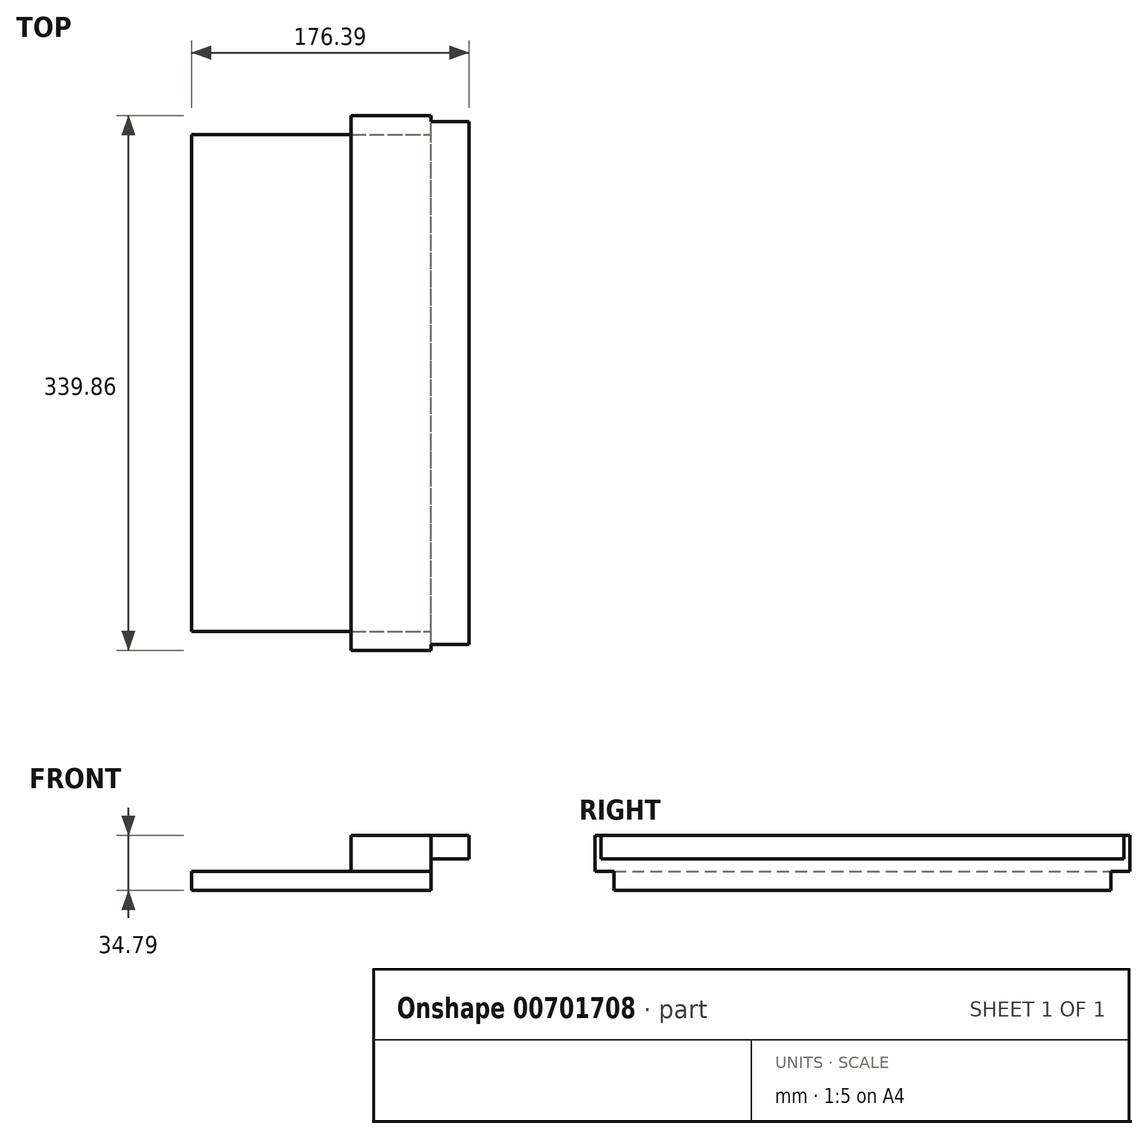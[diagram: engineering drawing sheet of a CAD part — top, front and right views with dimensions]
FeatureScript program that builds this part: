
annotation { "Feature Type Name" : "Feature", "Feature Type Description" : "" }
export const myFeature = defineFeature(function(context is Context, id is Id, definition is map)
    precondition{}
    {
        {
            var Q0;
            Q0=qCreatedBy(makeId("Front.planeOp"),FACE);
            var sketch = newSketch(context, id + "F0", { "sketchPlane" : qUnion([Q0])});
            skLineSegment(sketch, "E0", {"start": v(-72.73, 57.8) * mm, "end": v(-3.41, 57.8) * mm});
            skLineSegment(sketch, "E1", {"start": v(-3.41, 57.8) * mm, "end": v(-3.41, 3.04) * mm});
            skLineSegment(sketch, "E2", {"start": v(-3.41, 3.04) * mm, "end": v(-73.1, 3.04) * mm});
            skLineSegment(sketch, "E3", {"start": v(-73.1, 3.04) * mm, "end": v(-72.73, 57.8) * mm});
            skSolve(sketch);
        }
        {
            var Q0;
            Q0=makeQuery(id+"F0.imprint","IMPRINT",FACE,{"disambiguationData":[TD([[makeQuery(id+"F0.imprint","IMPRINT",EDGE,{"derivedFrom":sQuery(id+"F0.wireOp",EDGE,"E0")}),-1.0]])]});
            extrude(context, id + "F1", {"entities" : qUnion([Q0]), "depth" : 42.93 * mm, "offsetDistance" : 25.4 * mm});
        }
        {
            var Q0;
            Q0=qCreatedBy(makeId("Front.planeOp"),FACE);
            var sketch = newSketch(context, id + "F2", { "sketchPlane" : qUnion([Q0])});
            skCircle(sketch, "E4", {"center": v(-37.15, -45.63) * mm, "radius": 15.91 * mm});
            skSolve(sketch);
        }
        {
            var Q0;
            Q0=makeQuery(id+"F2.imprint","IMPRINT",FACE,{"disambiguationData":[TD([[makeQuery(id+"F2.imprint","IMPRINT",EDGE,{"derivedFrom":sQuery(id+"F2.wireOp",EDGE,"E4")}),1.0]])]});
            extrude(context, id + "F3", {"entities" : qUnion([Q0]), "depth" : 217.93 * mm, "offsetDistance" : 25.4 * mm});
        }
        {
            var Q0;
            Q0=makeQuery(id+"F3.opExtrude","SWEPT_BODY",BODY,{"disambiguationData":[OSD([sQuery(id+"F2.wireOp",EDGE,"E4")])]});
            var Q1;
            Q1=makeQuery(id+"F1.opExtrude","SWEPT_BODY",BODY,{"disambiguationData":[OSD([sQuery(id+"F0.wireOp",EDGE,"E0"),sQuery(id+"F0.wireOp",EDGE,"E1"),sQuery(id+"F0.wireOp",EDGE,"E2"),sQuery(id+"F0.wireOp",EDGE,"E3")])]});
            deleteBodies(context, id + "F4", {"entities" : qUnion([Q0, Q1])});
        }
        {
            var Q0;
            Q0=qCreatedBy(makeId("Front.planeOp"),FACE);
            var sketch = newSketch(context, id + "F5", { "sketchPlane" : qUnion([Q0])});
            skLineSegment(sketch, "E5.bottom", {"start": v(-75.76, 5.33) * mm, "end": v(76.44, 5.33) * mm});
            skLineSegment(sketch, "E5.top", {"start": v(-75.76, -6.76) * mm, "end": v(76.44, -6.76) * mm});
            skLineSegment(sketch, "E5.left", {"start": v(-75.76, 5.33) * mm, "end": v(-75.76, -6.76) * mm});
            skLineSegment(sketch, "E5.right", {"start": v(76.44, 5.33) * mm, "end": v(76.44, -6.76) * mm});
            skLineSegment(sketch, "E6.bottom", {"start": v(25.83, 28.03) * mm, "end": v(76.44, 28.03) * mm});
            skLineSegment(sketch, "E6.top", {"start": v(25.83, 5.33) * mm, "end": v(76.44, 5.33) * mm});
            skLineSegment(sketch, "E6.left", {"start": v(25.83, 28.03) * mm, "end": v(25.83, 5.33) * mm});
            skLineSegment(sketch, "E6.right", {"start": v(76.44, 28.03) * mm, "end": v(76.44, 5.33) * mm});
            skLineSegment(sketch, "E7.bottom", {"start": v(76.44, 28.03) * mm, "end": v(100.63, 28.03) * mm});
            skLineSegment(sketch, "E7.top", {"start": v(76.44, 13.33) * mm, "end": v(100.63, 13.33) * mm});
            skLineSegment(sketch, "E7.left", {"start": v(76.44, 13.33) * mm, "end": v(76.44, 28.03) * mm});
            skLineSegment(sketch, "E7.right", {"start": v(100.63, 13.33) * mm, "end": v(100.63, 28.03) * mm});
            skFitSpline(sketch, "E8", {"points": [v(-75.76, 5.33) * mm, v(25.83, 28.03) * mm], "startDerivative": vector(56.35, 60.24) * mm, "endDerivative": vector(106.28, -1.13) * mm});
            skSolve(sketch);
        }
        {
            var Q0;
            Q0=makeQuery(id+"F5.imprint","IMPRINT",FACE,{"disambiguationData":[TD([[makeQuery(id+"F5.imprint","IMPRINT",EDGE,{"derivedFrom":sQuery(id+"F5.wireOp",EDGE,"E6.bottom")}),-1.0]])]});
            var sketch = newSketch(context, id + "F6", { "sketchPlane" : qUnion([Q0])});
            skSolve(sketch);
        }
        {
            var Q0;
            Q0=makeQuery(id+"F6.imprint","IMPRINT",FACE,{"disambiguationData":[TD([[makeQuery(id+"F6.imprint","IMPRINT",EDGE,{"derivedFrom":makeQuery(id+"F5.imprint","IMPRINT",EDGE,{"derivedFrom":sQuery(id+"F5.wireOp",EDGE,"E6.bottom")})}),-1.0]])]});
            extrude(context, id + "F7", {"entities" : qUnion([Q0]), "endBound" : BoundingType.SYMMETRIC, "depth" : 339.85 * mm, "offsetDistance" : 25.4 * mm});
        }
        {
            var Q0;
            Q0=makeQuery(id+"F5.imprint","IMPRINT",FACE,{"disambiguationData":[TD([[makeQuery(id+"F5.imprint","IMPRINT",EDGE,{"derivedFrom":sQuery(id+"F5.wireOp",EDGE,"E5.bottom")}),-1.0]])]});
            var sketch = newSketch(context, id + "F8", { "sketchPlane" : qUnion([Q0])});
            skSolve(sketch);
        }
        {
            var Q0;
            Q0=makeQuery(id+"F8.imprint","IMPRINT",FACE,{"disambiguationData":[TD([[makeQuery(id+"F8.imprint","IMPRINT",EDGE,{"derivedFrom":makeQuery(id+"F5.imprint","IMPRINT",EDGE,{"derivedFrom":sQuery(id+"F5.wireOp",EDGE,"E5.bottom")})}),-1.0]])]});
            extrude(context, id + "F9", {"entities" : qUnion([Q0]), "operationType" : NewBodyOperationType.ADD, "endBound" : BoundingType.SYMMETRIC, "depth" : 315.47 * mm, "offsetDistance" : 25.4 * mm});
        }
        {
            var Q0;
            Q0=makeQuery(id+"F5.imprint","IMPRINT",FACE,{"disambiguationData":[TD([[makeQuery(id+"F5.imprint","IMPRINT",EDGE,{"derivedFrom":sQuery(id+"F5.wireOp",EDGE,"E7.bottom")}),-1.0]])]});
            var sketch = newSketch(context, id + "F10", { "sketchPlane" : qUnion([Q0])});
            skSolve(sketch);
        }
        {
            var Q0;
            Q0=makeQuery(id+"F10.imprint","IMPRINT",FACE,{"disambiguationData":[TD([[makeQuery(id+"F10.imprint","IMPRINT",EDGE,{"derivedFrom":makeQuery(id+"F5.imprint","IMPRINT",EDGE,{"derivedFrom":sQuery(id+"F5.wireOp",EDGE,"E7.bottom")})}),-1.0]])]});
            extrude(context, id + "F11", {"entities" : qUnion([Q0]), "operationType" : NewBodyOperationType.ADD, "endBound" : BoundingType.SYMMETRIC, "depth" : 332.23 * mm, "offsetDistance" : 25.4 * mm});
        }
    });
